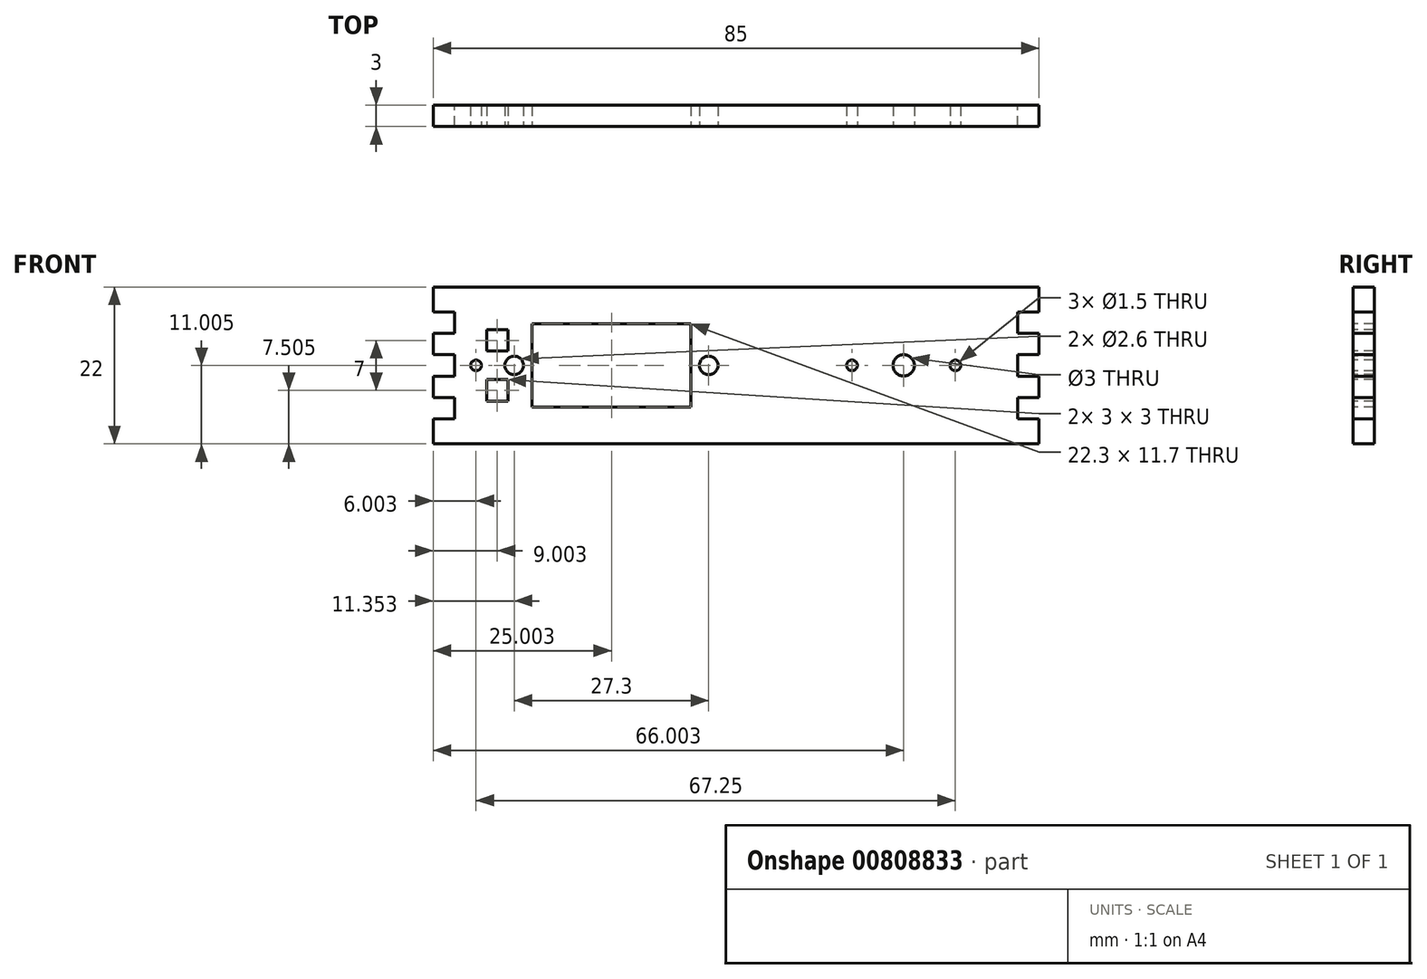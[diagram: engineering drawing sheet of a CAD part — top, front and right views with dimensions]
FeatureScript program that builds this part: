
annotation { "Feature Type Name" : "Feature", "Feature Type Description" : "" }
export const myFeature = defineFeature(function(context is Context, id is Id, definition is map)
    precondition{}
    {
        {
            var Q0;
            Q0=qCreatedBy(makeId("Front.planeOp"),FACE);
            var sketch = newSketch(context, id + "F0", { "sketchPlane" : qUnion([Q0])});
            skLineSegment(sketch, "E0.bottom", {"start": v(-42.09, 16.9) * mm, "end": v(42.91, 16.9) * mm});
            skLineSegment(sketch, "E0.top", {"start": v(-42.09, -5.1) * mm, "end": v(42.91, -5.1) * mm});
            skLineSegment(sketch, "E0.left", {"start": v(-42.09, 16.9) * mm, "end": v(-42.09, -5.1) * mm});
            skLineSegment(sketch, "E0.right", {"start": v(42.91, 16.9) * mm, "end": v(42.91, -5.1) * mm});
            skPoint(sketch, "E0.middle", {"position": v(0.41, 5.9) * mm});
            skLineSegment(sketch, "E1.bottom", {"start": v(45.91, 4.4) * mm, "end": v(39.91, 4.4) * mm});
            skLineSegment(sketch, "E1.top", {"start": v(45.91, 7.4) * mm, "end": v(39.91, 7.4) * mm});
            skLineSegment(sketch, "E1.left", {"start": v(45.91, 4.4) * mm, "end": v(45.91, 7.4) * mm});
            skLineSegment(sketch, "E1.right", {"start": v(39.91, 4.4) * mm, "end": v(39.91, 7.4) * mm});
            skPoint(sketch, "E1.middle", {"position": v(42.91, 5.9) * mm});
            skLineSegment(sketch, "E2.bottom", {"start": v(45.91, 10.4) * mm, "end": v(39.91, 10.4) * mm});
            skLineSegment(sketch, "E2.top", {"start": v(45.91, 13.4) * mm, "end": v(39.91, 13.4) * mm});
            skLineSegment(sketch, "E2.left", {"start": v(45.91, 10.4) * mm, "end": v(45.91, 13.4) * mm});
            skLineSegment(sketch, "E2.right", {"start": v(39.91, 10.4) * mm, "end": v(39.91, 13.4) * mm});
            skPoint(sketch, "E2.middle", {"position": v(42.91, 11.9) * mm});
            skLineSegment(sketch, "E3.bottom", {"start": v(45.91, -1.6) * mm, "end": v(39.91, -1.6) * mm});
            skLineSegment(sketch, "E3.top", {"start": v(45.91, 1.4) * mm, "end": v(39.91, 1.4) * mm});
            skLineSegment(sketch, "E3.left", {"start": v(45.91, -1.6) * mm, "end": v(45.91, 1.4) * mm});
            skLineSegment(sketch, "E3.right", {"start": v(39.91, -1.6) * mm, "end": v(39.91, 1.4) * mm});
            skPoint(sketch, "E3.middle", {"position": v(42.91, -0.1) * mm});
            skLineSegment(sketch, "E4", {"start": v(0.41, 5.9) * mm, "end": v(0.41, 9.96) * mm});
            skLineSegment(sketch, "E5.MirrorCS", {"start": v(-45.09, 4.4) * mm, "end": v(-39.09, 4.4) * mm});
            skLineSegment(sketch, "E6.MirrorCS", {"start": v(-39.09, 4.4) * mm, "end": v(-39.09, 7.4) * mm});
            skLineSegment(sketch, "E7.MirrorCS", {"start": v(-45.09, 7.4) * mm, "end": v(-39.09, 7.4) * mm});
            skLineSegment(sketch, "E8.MirrorCS", {"start": v(-45.09, 4.4) * mm, "end": v(-45.09, 7.4) * mm});
            skLineSegment(sketch, "E9.MirrorCS", {"start": v(-45.09, 1.4) * mm, "end": v(-39.09, 1.4) * mm});
            skLineSegment(sketch, "E10.MirrorCS", {"start": v(-45.09, -1.6) * mm, "end": v(-39.09, -1.6) * mm});
            skLineSegment(sketch, "E11.MirrorCS", {"start": v(-39.09, -1.6) * mm, "end": v(-39.09, 1.4) * mm});
            skLineSegment(sketch, "E12.MirrorCS", {"start": v(-45.09, -1.6) * mm, "end": v(-45.09, 1.4) * mm});
            skLineSegment(sketch, "E13.MirrorCS", {"start": v(-45.09, 10.4) * mm, "end": v(-39.09, 10.4) * mm});
            skLineSegment(sketch, "E14.MirrorCS", {"start": v(-39.09, 10.4) * mm, "end": v(-39.09, 13.4) * mm});
            skLineSegment(sketch, "E15.MirrorCS", {"start": v(-45.09, 13.4) * mm, "end": v(-39.09, 13.4) * mm});
            skLineSegment(sketch, "E16.MirrorCS", {"start": v(-45.09, 10.4) * mm, "end": v(-45.09, 13.4) * mm});
            skSolve(sketch);
        }
        {
            var Q0;
            {var subQ21=sQuery(id+"F0.wireOp",EDGE,"E0.bottom");Q0=makeQuery(id+"F0.imprint","IMPRINT",FACE,{"disambiguationData":[TD([[makeQuery(id+"F0.imprint","IMPRINT",EDGE,{"derivedFrom":subQ21}),-1.0]])]});}
            extrude(context, id + "F1", {"entities" : qUnion([Q0]), "depth" : 3 * mm, "offsetDistance" : 25 * mm});
        }
        {
            var Q0;
            Q0=makeQuery(id+"F1.opExtrude","CAP_FACE",FACE,{"disambiguationData":[OSD([sQuery(id+"F0.wireOp",EDGE,"E0.bottom"),sQuery(id+"F0.wireOp",EDGE,"E0.top"),sQuery(id+"F0.wireOp",EDGE,"E0.left"),sQuery(id+"F0.wireOp",EDGE,"E0.right"),sQuery(id+"F0.wireOp",EDGE,"E1.bottom"),sQuery(id+"F0.wireOp",EDGE,"E1.top"),sQuery(id+"F0.wireOp",EDGE,"E1.right"),sQuery(id+"F0.wireOp",EDGE,"E2.bottom"),sQuery(id+"F0.wireOp",EDGE,"E2.top"),sQuery(id+"F0.wireOp",EDGE,"E2.right"),sQuery(id+"F0.wireOp",EDGE,"E3.bottom"),sQuery(id+"F0.wireOp",EDGE,"E3.top"),sQuery(id+"F0.wireOp",EDGE,"E3.right"),sQuery(id+"F0.wireOp",EDGE,"E5.MirrorCS"),sQuery(id+"F0.wireOp",EDGE,"E6.MirrorCS"),sQuery(id+"F0.wireOp",EDGE,"E7.MirrorCS"),sQuery(id+"F0.wireOp",EDGE,"E9.MirrorCS"),sQuery(id+"F0.wireOp",EDGE,"E10.MirrorCS"),sQuery(id+"F0.wireOp",EDGE,"E11.MirrorCS"),sQuery(id+"F0.wireOp",EDGE,"E13.MirrorCS"),sQuery(id+"F0.wireOp",EDGE,"E14.MirrorCS"),sQuery(id+"F0.wireOp",EDGE,"E15.MirrorCS")])],"isStart":false});
            var sketch = newSketch(context, id + "F2", { "sketchPlane" : qUnion([Q0])});
            skLineSegment(sketch, "E17.bottom", {"start": v(-5.94, 0.05) * mm, "end": v(-28.24, 0.05) * mm});
            skLineSegment(sketch, "E17.top", {"start": v(-5.94, 11.75) * mm, "end": v(-28.24, 11.75) * mm});
            skLineSegment(sketch, "E17.left", {"start": v(-5.94, 0.05) * mm, "end": v(-5.94, 11.75) * mm});
            skLineSegment(sketch, "E17.right", {"start": v(-28.24, 0.05) * mm, "end": v(-28.24, 11.75) * mm});
            skPoint(sketch, "E17.middle", {"position": v(-17.09, 5.9) * mm});
            skCircle(sketch, "E18", {"center": v(23.91, 5.9) * mm, "radius": 1.5 * mm});
            skCircle(sketch, "E19", {"center": v(16.66, 5.9) * mm, "radius": 0.75 * mm});
            skCircle(sketch, "E20", {"center": v(31.16, 5.9) * mm, "radius": 0.75 * mm});
            skCircle(sketch, "E21", {"center": v(-3.44, 5.9) * mm, "radius": 1.3 * mm});
            skCircle(sketch, "E22", {"center": v(-30.74, 5.9) * mm, "radius": 1.3 * mm});
            skPoint(sketch, "E22.centerSnap0", {"position": v(-28.24, 5.9) * mm});
            skCircle(sketch, "E23", {"center": v(-36.09, 5.9) * mm, "radius": 0.75 * mm});
            skPoint(sketch, "E23.centerSnap0", {"position": v(-39.09, 5.9) * mm});
            skLineSegment(sketch, "E24.bottom", {"start": v(-31.59, 0.9) * mm, "end": v(-34.59, 0.9) * mm});
            skLineSegment(sketch, "E24.top", {"start": v(-31.59, 3.9) * mm, "end": v(-34.59, 3.9) * mm});
            skLineSegment(sketch, "E24.left", {"start": v(-31.59, 0.9) * mm, "end": v(-31.59, 3.9) * mm});
            skLineSegment(sketch, "E24.right", {"start": v(-34.59, 0.9) * mm, "end": v(-34.59, 3.9) * mm});
            skPoint(sketch, "E24.middle", {"position": v(-33.09, 2.4) * mm});
            skLineSegment(sketch, "E25.bottom", {"start": v(-31.59, 7.9) * mm, "end": v(-34.59, 7.9) * mm});
            skLineSegment(sketch, "E25.top", {"start": v(-31.59, 10.9) * mm, "end": v(-34.59, 10.9) * mm});
            skLineSegment(sketch, "E25.left", {"start": v(-31.59, 7.9) * mm, "end": v(-31.59, 10.9) * mm});
            skLineSegment(sketch, "E25.right", {"start": v(-34.59, 7.9) * mm, "end": v(-34.59, 10.9) * mm});
            skPoint(sketch, "E25.middle", {"position": v(-33.09, 9.4) * mm});
            skSolve(sketch);
        }
        {
            var Q0;
            Q0=qSketchRegion(id+"F2",true);
            extrude(context, id + "F3", {"entities" : qUnion([Q0]), "operationType" : NewBodyOperationType.REMOVE, "oppositeDirection" : true, "depth" : 25 * mm, "offsetDistance" : 25 * mm});
        }
    });
